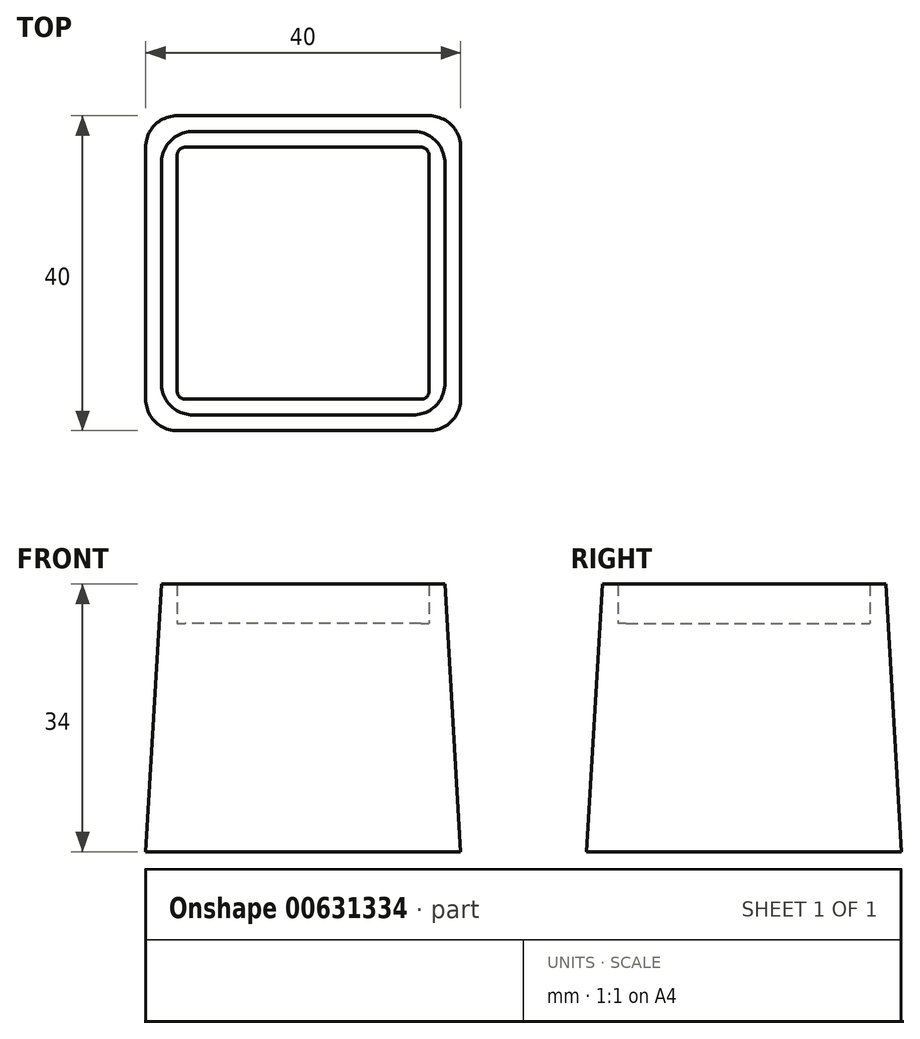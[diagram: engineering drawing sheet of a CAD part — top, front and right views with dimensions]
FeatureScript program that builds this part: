
annotation { "Feature Type Name" : "Feature", "Feature Type Description" : "" }
export const myFeature = defineFeature(function(context is Context, id is Id, definition is map)
    precondition{}
    {
        {
            var Q0;
            Q0=qCreatedBy(makeId("Top.planeOp"),FACE);
            var sketch = newSketch(context, id + "F0", { "sketchPlane" : qUnion([Q0])});
            skLineSegment(sketch, "E0.bottom", {"start": v(16, -16) * mm, "end": v(-16, -16) * mm});
            skLineSegment(sketch, "E0.top", {"start": v(16, 16) * mm, "end": v(-16, 16) * mm});
            skLineSegment(sketch, "E0.left", {"start": v(16, -16) * mm, "end": v(16, 16) * mm});
            skLineSegment(sketch, "E0.right", {"start": v(-16, -16) * mm, "end": v(-16, 16) * mm});
            skPoint(sketch, "E0.middle", {"position": v(0, 0) * mm});
            skSolve(sketch);
        }
        {
            var Q0;
            Q0=qCreatedBy(makeId("Front.planeOp"),FACE);
            var sketch = newSketch(context, id + "F1", { "sketchPlane" : qUnion([Q0])});
            skLineSegment(sketch, "E1", {"start": v(0, 0) * mm, "end": v(0, -29) * mm});
            skSolve(sketch);
        }
        {
            var Q0;
            Q0=qCreatedBy(makeId("Top.planeOp"),FACE);
            cPlane(context, id + "F2", {"entities" : qUnion([Q0]), "cplaneType" : CPlaneType.OFFSET, "offset" : 5 * mm, "width" : 150 * mm, "height" : 150 * mm});
        }
        {
            var Q0;
            Q0=qCreatedBy(makeId("Top.planeOp"),FACE);
            var Q1;
            Q1=sQuery(id+"F1.wireOp",VERTEX,"E1.end");
            cPlane(context, id + "F3", {"entities" : qUnion([Q0, Q1]), "cplaneType" : CPlaneType.PLANE_POINT, "offset" : 25 * mm, "width" : 150 * mm, "height" : 150 * mm});
        }
        {
            var Q0;
            Q0=qCreatedBy(id+"F3.planeOp",FACE);
            var sketch = newSketch(context, id + "F4", { "sketchPlane" : qUnion([Q0])});
            skLineSegment(sketch, "E2.bottom", {"start": v(20, 20) * mm, "end": v(-20, 20) * mm});
            skLineSegment(sketch, "E2.top", {"start": v(20, -20) * mm, "end": v(-20, -20) * mm});
            skLineSegment(sketch, "E2.left", {"start": v(20, 20) * mm, "end": v(20, -20) * mm});
            skLineSegment(sketch, "E2.right", {"start": v(-20, 20) * mm, "end": v(-20, -20) * mm});
            skPoint(sketch, "E2.middle", {"position": v(0, 0) * mm});
            skSolve(sketch);
        }
        {
            var Q0;
            Q0=qCreatedBy(id+"F2.planeOp",FACE);
            var sketch = newSketch(context, id + "F5", { "sketchPlane" : qUnion([Q0])});
            skLineSegment(sketch, "E3.bottom", {"start": v(18, 18) * mm, "end": v(-18, 18) * mm});
            skLineSegment(sketch, "E3.top", {"start": v(18, -18) * mm, "end": v(-18, -18) * mm});
            skLineSegment(sketch, "E3.left", {"start": v(18, 18) * mm, "end": v(18, -18) * mm});
            skLineSegment(sketch, "E3.right", {"start": v(-18, 18) * mm, "end": v(-18, -18) * mm});
            skPoint(sketch, "E3.middle", {"position": v(0, 0) * mm});
            skSolve(sketch);
        }
        {
            var Q0;
            Q0=makeQuery(id+"F4.imprint","IMPRINT",FACE,{"disambiguationData":[TD([[makeQuery(id+"F4.imprint","IMPRINT",EDGE,{"derivedFrom":sQuery(id+"F4.wireOp",EDGE,"E2.bottom")}),1.0]])]});
            var Q1;
            Q1=makeQuery(id+"F5.imprint","IMPRINT",FACE,{"disambiguationData":[TD([[makeQuery(id+"F5.imprint","IMPRINT",EDGE,{"derivedFrom":sQuery(id+"F5.wireOp",EDGE,"E3.bottom")}),1.0]])]});
            loft(context, id + "F6", {"sheetProfilesArray" : [{ "sheetProfileEntities" : qUnion([Q0]) }, { "sheetProfileEntities" : qUnion([Q1]) }]});
        }
        {
            var Q0;
            Q0 = qSketchRegion(id + "F0", true);
            extrude(context, id + "F7", {"entities" : qUnion([Q0]), "operationType" : NewBodyOperationType.REMOVE, "depth" : 25 * mm, "offsetDistance" : 25 * mm});
        }
        {
            var Q0;
            Q0=makeQuery(id+"F6.opLoft","SWEPT_EDGE",EDGE,{"disambiguationData":[OSD([sQuery(id+"F4.wireOp",EDGE,"E2.top"),sQuery(id+"F4.wireOp",EDGE,"E2.left"),sQuery(id+"F5.wireOp",EDGE,"E3.top"),sQuery(id+"F5.wireOp",EDGE,"E3.left")])]});
            var Q1;
            Q1=makeQuery(id+"F6.opLoft","SWEPT_EDGE",EDGE,{"disambiguationData":[OSD([sQuery(id+"F4.wireOp",EDGE,"E2.bottom"),sQuery(id+"F4.wireOp",EDGE,"E2.left"),sQuery(id+"F5.wireOp",EDGE,"E3.bottom"),sQuery(id+"F5.wireOp",EDGE,"E3.left")])]});
            var Q2;
            Q2=makeQuery(id+"F6.opLoft","SWEPT_EDGE",EDGE,{"disambiguationData":[OSD([sQuery(id+"F4.wireOp",EDGE,"E2.top"),sQuery(id+"F4.wireOp",EDGE,"E2.right"),sQuery(id+"F5.wireOp",EDGE,"E3.top"),sQuery(id+"F5.wireOp",EDGE,"E3.right")])]});
            var Q3;
            Q3=makeQuery(id+"F6.opLoft","SWEPT_EDGE",EDGE,{"disambiguationData":[OSD([sQuery(id+"F4.wireOp",EDGE,"E2.bottom"),sQuery(id+"F4.wireOp",EDGE,"E2.right"),sQuery(id+"F5.wireOp",EDGE,"E3.bottom"),sQuery(id+"F5.wireOp",EDGE,"E3.right")])]});
            fillet(context, id + "F8", {"entities" : qUnion([Q0, Q1, Q2, Q3]), "radius" : 4 * mm, "tangentPropagation" : true, "allowEdgeOverflow" : false});
        }
        {
            var Q0;
            Q0=makeQuery(id+"F7.boolean.opBoolean","COPY",EDGE,{"derivedFrom":makeQuery(id+"F7.opExtrude","SWEPT_EDGE",EDGE,{"disambiguationData":[OSD([sQuery(id+"F0.wireOp",EDGE,"E0.top"),sQuery(id+"F0.wireOp",EDGE,"E0.right")])]})});
            var Q1;
            Q1=makeQuery(id+"F7.boolean.opBoolean","COPY",EDGE,{"derivedFrom":makeQuery(id+"F7.opExtrude","SWEPT_EDGE",EDGE,{"disambiguationData":[OSD([sQuery(id+"F0.wireOp",EDGE,"E0.top"),sQuery(id+"F0.wireOp",EDGE,"E0.left")])]})});
            var Q2;
            Q2=makeQuery(id+"F7.boolean.opBoolean","COPY",EDGE,{"derivedFrom":makeQuery(id+"F7.opExtrude","SWEPT_EDGE",EDGE,{"disambiguationData":[OSD([sQuery(id+"F0.wireOp",EDGE,"E0.bottom"),sQuery(id+"F0.wireOp",EDGE,"E0.left")])]})});
            var Q3;
            Q3=makeQuery(id+"F7.boolean.opBoolean","COPY",EDGE,{"derivedFrom":makeQuery(id+"F7.opExtrude","SWEPT_EDGE",EDGE,{"disambiguationData":[OSD([sQuery(id+"F0.wireOp",EDGE,"E0.bottom"),sQuery(id+"F0.wireOp",EDGE,"E0.right")])]})});
            fillet(context, id + "F9", {"entities" : qUnion([Q0, Q1, Q2, Q3]), "radius" : 1 * mm, "tangentPropagation" : true, "allowEdgeOverflow" : false});
        }
    });
